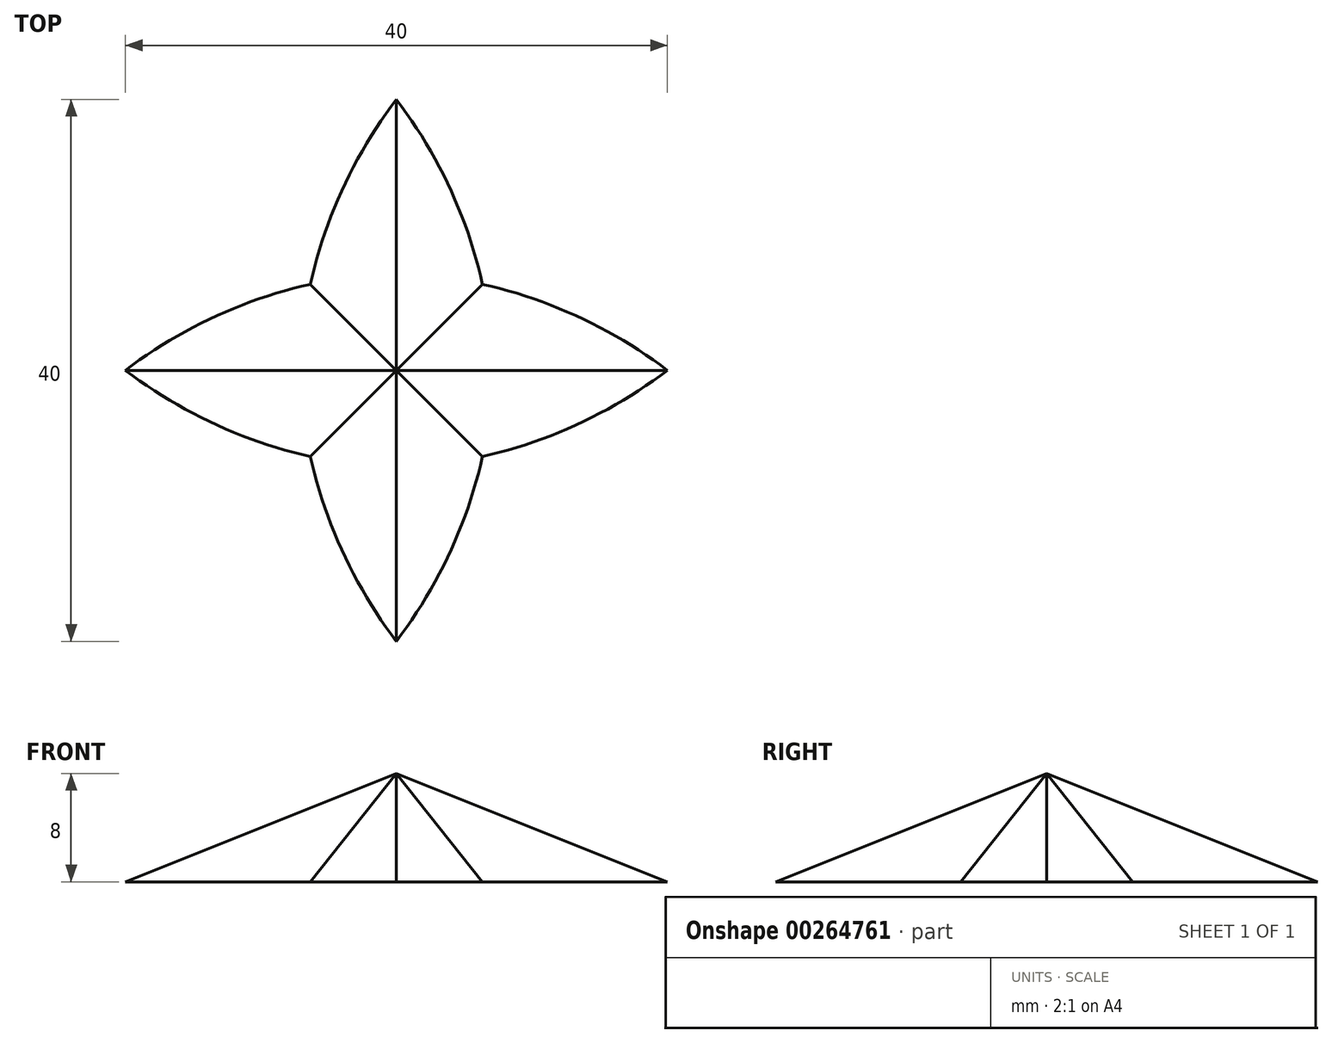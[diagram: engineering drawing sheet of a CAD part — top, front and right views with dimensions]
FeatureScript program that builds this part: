
annotation { "Feature Type Name" : "Feature", "Feature Type Description" : "" }
export const myFeature = defineFeature(function(context is Context, id is Id, definition is map)
    precondition{}
    {
        {
            var Q0;
            Q0=qCreatedBy(makeId("Top.planeOp"),FACE);
            var sketch = newSketch(context, id + "F0", { "sketchPlane" : qUnion([Q0])});
            skLineSegment(sketch, "E0", {"start": v(0, 25.42) * mm, "end": v(0, -24.58) * mm, "construction": true});
            skSolve(sketch);
        }
        {
            var Q0;
            Q0=qCreatedBy(makeId("Top.planeOp"),FACE);
            var sketch = newSketch(context, id + "F1", { "sketchPlane" : qUnion([Q0])});
            skFitSpline(sketch, "E1", {"points": [v(0, 20) * mm, v(-6.35, 6.35) * mm], "startDerivative": vector(-9, -11.8) * mm, "endDerivative": vector(-3.16, -14.56) * mm});
            skLineSegment(sketch, "E2", {"start": v(-6.35, 6.35) * mm, "end": v(0, 0) * mm, "construction": true});
            skFitSpline(sketch, "E3.MirrorCS", {"points": [v(0, 20) * mm, v(6.35, 6.35) * mm], "startDerivative": vector(9, -11.8) * mm, "endDerivative": vector(3.16, -14.56) * mm});
            skLineSegment(sketch, "E4.MirrorCS", {"start": v(6.35, 6.35) * mm, "end": v(0, 0) * mm, "construction": true});
            skFitSpline(sketch, "E5.MirrorCS", {"points": [v(-20, 0) * mm, v(-6.35, 6.35) * mm], "startDerivative": vector(11.8, 9) * mm, "endDerivative": vector(14.56, 3.16) * mm});
            skFitSpline(sketch, "E6.MirrorCS", {"points": [v(-20, 0) * mm, v(-6.35, -6.35) * mm], "startDerivative": vector(11.8, -9) * mm, "endDerivative": vector(14.56, -3.16) * mm});
            skFitSpline(sketch, "E7.MirrorCS", {"points": [v(20, 0) * mm, v(6.35, 6.35) * mm], "startDerivative": vector(-11.8, 9) * mm, "endDerivative": vector(-14.56, 3.16) * mm});
            skFitSpline(sketch, "E8.MirrorCS", {"points": [v(20, 0) * mm, v(6.35, -6.35) * mm], "startDerivative": vector(-11.8, -9) * mm, "endDerivative": vector(-14.56, -3.16) * mm});
            skFitSpline(sketch, "E9.MirrorCS", {"points": [v(0, -20) * mm, v(6.35, -6.35) * mm], "startDerivative": vector(9, 11.8) * mm, "endDerivative": vector(3.16, 14.56) * mm});
            skFitSpline(sketch, "E10.MirrorCS", {"points": [v(0, -20) * mm, v(-6.35, -6.35) * mm], "startDerivative": vector(-9, 11.8) * mm, "endDerivative": vector(-3.16, 14.56) * mm});
            skLineSegment(sketch, "E11", {"start": v(0, 20) * mm, "end": v(0, -20) * mm, "construction": true});
            skSolve(sketch);
        }
        {
            var Q0;
            Q0=qCreatedBy(makeId("Top.planeOp"),FACE);
            cPlane(context, id + "F2", {"entities" : qUnion([Q0]), "cplaneType" : CPlaneType.OFFSET, "offset" : 8 * mm, "width" : 150 * mm, "height" : 150 * mm});
        }
        {
            var Q0;
            Q0=qCreatedBy(id+"F2.planeOp",FACE);
            var sketch = newSketch(context, id + "F3", { "sketchPlane" : qUnion([Q0])});
            skPoint(sketch, "E12", {"position": v(0, 0) * mm});
            skSolve(sketch);
        }
        {
            var Q0;
            Q0=makeQuery(id+"F1.imprint","IMPRINT",FACE,{"disambiguationData":[TD([[makeQuery(id+"F1.imprint","IMPRINT",EDGE,{"derivedFrom":sQuery(id+"F1.wireOp",EDGE,"E1")}),1.0]])]});
            var Q1;
            Q1=sQuery(id+"F3.wireOp",VERTEX,"E12");
            loft(context, id + "F4", {"sheetProfilesArray" : [{ "sheetProfileEntities" : qUnion([Q0]) }, { "sheetProfileEntities" : qUnion([Q1]) }]});
        }
    });
